# Revit family: 2059270 Sylvania Lighting Fixture BEACON TUNE II SPOT SSC01 LS3 BLACK
name_source: partatom
category: Lighting Fixtures
revit_build: Autodesk Revit 2017 (Build: 20190507_1515(x64)
units: mm (PartAtom-declared; Revit-internal decimal feet)

## family parameters
Cut with Voids When Loaded = No
Host = Face
Light Source = No
OmniClass Number = 23.80.70.00
OmniClass Title = Lighting
Part Type = Normal
Room Calculation Point = No
Round Connector Dimension = Use Diameter
Shared = No

## types (1)
- 2059270 BEACON TUNE II SPOT SSC01 LS3 BLACK
    Apparent Load = 19 VA
    Assembly Code = D5020200
    Cost = 0 $
    Default Elevation = 1219 mm
    Description = Integrated LED spotlight, Black RAL9005, compact and minimalist design, ideal for retail, display, museum and gallery applications, die-cast aluminium body, passive cooling heatsink, beam angle: 26° (spot) optics: Fresnel lens for controlled beam, color temperature: 1800-6500K Tuneable white , total system power: 19W, total fixture output: 1008lm, luminaire efficacy: 53lm/W, LOR: 100%, colour rendering: Ra: 90 typical, LED Chromaticity: 3step MacAdam ellipse, lifetime: >50,000hours at L70B50, energy class: A++, A+, A, IR/UV free light source without heat radiation, operating voltage: 220-240V / 50-60Hz, electronic driver, dimmable via SylSmart SSC Bluetooth, power factor: 0.9 electrical protection: Class I, 3-circuit track adaptor suitable for Concord Lytespan 3 track, ingress protection rating: IP20, suitable for internal environment only, horizontal rotation: 355°, vertical tilt: 90°, dimensions: Ø79x156x167mm, weight: 0.96kg.
    Height = 156 mm  [stored 0.511811 ft]
    Keynote = 0
    Length = 122 mm
    Manufacturer = Feilo Sylvania
    Material_1_SYL = <By Category>
    Material_2_SYL = <By Category>
    Material_3_SYL = <By Category>
    Material_4_SYL = <By Category>
    Model = BEACON TUNE II SPOT SSC01 LS3 BLACK
    Type Image = <None>
    URL = http://www.sylvania-lighting.com
    Width = 140 mm

note: [stored X ft] marks values corroborated as IEEE doubles in the binary element streams (Revit-internal decimal feet)

## geometry (parser evidence)
native form markers: Sweep x6
no freeform markers — native parametric forms only
